# Revit family: KEUCO_14914010000_
name_source: partatom
category: Generic Models
revit_build: Autodesk Revit 2016 (Build: 20150220_1215(x64)
units: mm (PartAtom-declared; Revit-internal decimal feet)

## family parameters
Always vertical = No
Can host rebar = No
Cut with Voids When Loaded = No
Part Type = Normal
Room Calculation Point = No
Round Connector Dimension = Use Diameter
Shared = No
Work Plane-Based = Yes

## types (3) — shared parameters
Default Elevation = 1219 mm
Description = --
Manufacturer = KEUCO
Serie = Plan
Stange Breite = 50 mm  [stored 0.164042 ft]
URL = https://www.keuco.com
Verwendung = BI / DU / GWC / WA / WP
zero-valued in all types: Gewicht

## per-type parameters (varying)
| type | Ausschreibungstext | Material |
| 14914010000 | KEUCO PLAN Handtuchhaken 14914010000
Hochglanzverchromter Handtuchhaken 
in ästhetischem, funktionalem Design
mit runder Rosettenkappe, Durchmesser 55 mm
leicht zu reinigen
Ausladung 51 mm
Der Handtuchhaken wird verdeckt angebracht
Lieferung inkl. korrosionsfreiem Befestigungsmaterial | Verchromt |
| 14914070000 | KEUCO PLAN Handtuchhaken 14914070000
Handtuchhalter aus hochwertigem Edelstahl 
in ästhetischem, funktionalem Design 
mit runder Rosettenkappe, Durchmesser 55 mm
leicht zu reinigen
Ausladung 51 mm
Der Handtuchhaken wird verdeckt angebracht
Lieferung inkl. korrosionsfreiem Befestigungsmaterial | Edelstahl |
| 14914170000 | KEUCO PLAN Handtuchhaken 14914170000
Handtuchhaken aus 
silber-eloxiertem Aluminium (E6 EV1)/verchromt 
in ästhetischem, funktionalem Design 
mit runder Rosettenkappe, Durchmesser 55 mm
hochglanzverchromtes Abschlussstück
leicht zu reinigen
Ausladung 51 mm
Der Handtuchhaken wird verdeckt angebracht
Lieferung inkl. korrosionsfreiem Befestigungsmaterial | Aluminium silber-eloxiert (E6 EV1) |

note: column(s) folded — value = type name in every type: Artikelnummer

note: [stored X ft] marks values corroborated as IEEE doubles in the binary element streams (Revit-internal decimal feet)

## geometry (parser evidence)
native form markers: Sweep x2
no freeform markers — native parametric forms only
